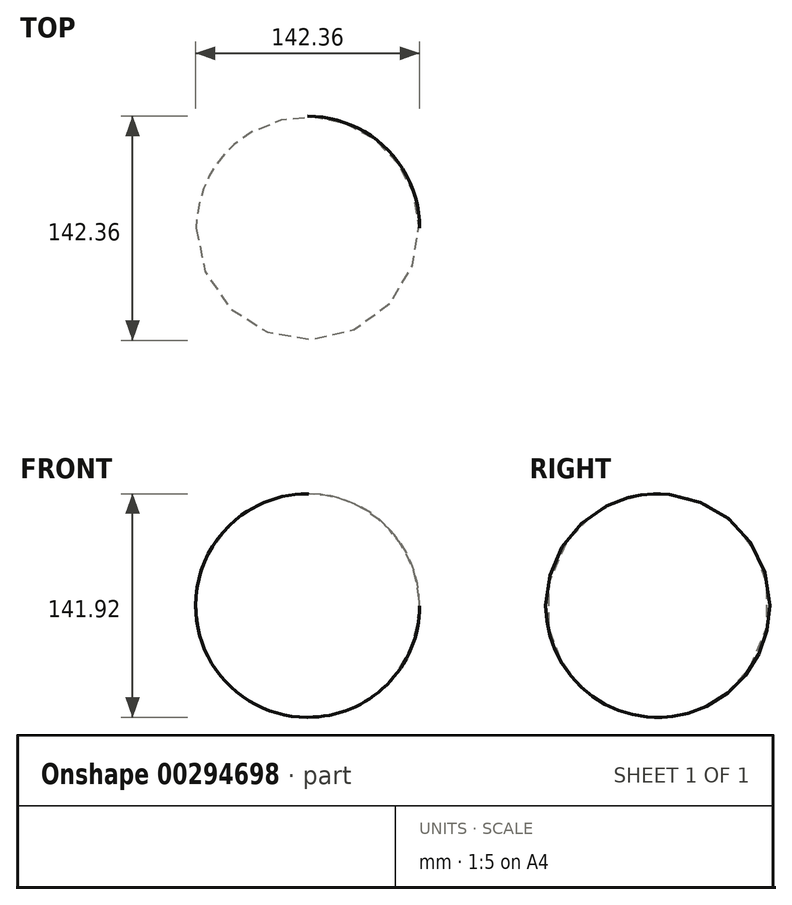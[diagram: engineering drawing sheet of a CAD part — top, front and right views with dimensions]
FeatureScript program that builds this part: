
annotation { "Feature Type Name" : "Feature", "Feature Type Description" : "" }
export const myFeature = defineFeature(function(context is Context, id is Id, definition is map)
    precondition{}
    {
        {
            var Q0;
            Q0=qCreatedBy(makeId("Top.planeOp"),FACE);
            var sketch = newSketch(context, id + "F0", { "sketchPlane" : qUnion([Q0])});
            skArc(sketch, "E0", {"start": v(22.56, 0) * mm, "mid": v(0, 22.56) * mm, "end": v(-22.56, 0) * mm});
            skLineSegment(sketch, "E1", {"start": v(-22.56, 0) * mm, "end": v(22.56, 0) * mm});
            skSolve(sketch);
        }
        {
            var Q0;
            Q0 = qSketchRegion(id + "F0", true);
            var Q1;
            Q1=sQuery(id+"F0.wireOp",EDGE,"E1");
            revolve(context, id + "F1", {"entities" : qUnion([Q0]), "axis" : qUnion([Q1]), "revolveType" : RevolveType.FULL});
        }
        {
            var Q0;
            Q0=qCreatedBy(makeId("Front.planeOp"),FACE);
            var sketch = newSketch(context, id + "F2", { "sketchPlane" : qUnion([Q0])});
            skArc(sketch, "E2", {"start": v(0, -70.96) * mm, "mid": v(70.96, -0.22) * mm, "end": v(0.44, 70.96) * mm});
            skLineSegment(sketch, "E3", {"start": v(0.44, 70.96) * mm, "end": v(0, -70.96) * mm});
            skSolve(sketch);
        }
        {
            var Q0;
            Q0=makeQuery(id+"F2.imprint","IMPRINT",FACE,{"disambiguationData":[TD([[makeQuery(id+"F2.imprint","IMPRINT",EDGE,{"derivedFrom":sQuery(id+"F2.wireOp",EDGE,"E2")}),1.0]])]});
            var Q1;
            Q1=sQuery(id+"F2.wireOp",EDGE,"E3");
            revolve(context, id + "F3", {"operationType" : NewBodyOperationType.ADD, "entities" : qUnion([Q0]), "axis" : qUnion([Q1]), "revolveType" : RevolveType.FULL});
        }
    });
